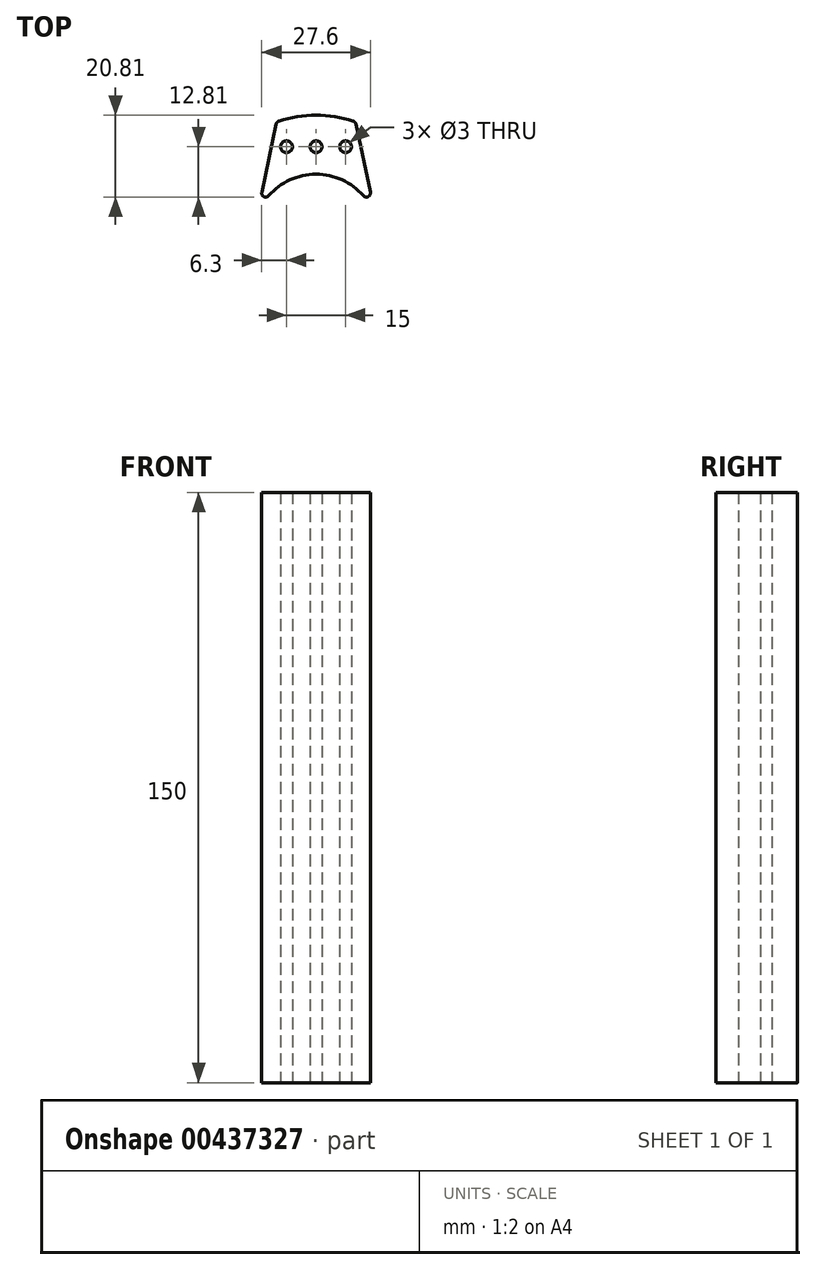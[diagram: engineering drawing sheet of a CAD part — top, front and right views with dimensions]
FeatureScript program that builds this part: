
annotation { "Feature Type Name" : "Feature", "Feature Type Description" : "" }
export const myFeature = defineFeature(function(context is Context, id is Id, definition is map)
    precondition{}
    {
        {
            var Q0;
            Q0=qCreatedBy(makeId("Top.planeOp"),FACE);
            var sketch = newSketch(context, id + "F0", { "sketchPlane" : qUnion([Q0])});
            skArc(sketch, "E0", {"start": v(12.04, 10.53) * mm, "mid": v(0, 16) * mm, "end": v(-12.04, 10.53) * mm});
            skLineSegment(sketch, "E1", {"start": v(-10.12, 28.78) * mm, "end": v(-13.77, 11.4) * mm});
            skLineSegment(sketch, "E2", {"start": v(10.12, 28.78) * mm, "end": v(13.77, 11.4) * mm});
            skArc(sketch, "E3.trimOffspring", {"start": v(9.44, 29.53) * mm, "mid": v(0, 31) * mm, "end": v(-9.44, 29.53) * mm});
            skPoint(sketch, "E4.visualSharp", {"position": v(-15, 5.57) * mm});
            skArc(sketch, "E4.filletArc", {"start": v(-13.77, 11.4) * mm, "mid": v(-13.24, 10.3) * mm, "end": v(-12.04, 10.53) * mm});
            skPoint(sketch, "E5.visualSharp", {"position": v(15, 5.57) * mm});
            skArc(sketch, "E5.filletArc", {"start": v(12.04, 10.53) * mm, "mid": v(13.24, 10.3) * mm, "end": v(13.77, 11.4) * mm});
            skPoint(sketch, "E6.visualSharp", {"position": v(-10, 29.34) * mm});
            skArc(sketch, "E6.filletArc", {"start": v(-9.44, 29.53) * mm, "mid": v(-9.88, 29.24) * mm, "end": v(-10.12, 28.78) * mm});
            skPoint(sketch, "E7.visualSharp", {"position": v(10, 29.34) * mm});
            skArc(sketch, "E7.filletArc", {"start": v(10.12, 28.78) * mm, "mid": v(9.88, 29.24) * mm, "end": v(9.44, 29.53) * mm});
            skCircle(sketch, "E8", {"center": v(0, 23) * mm, "radius": 1.5 * mm});
            skPoint(sketch, "E8.centerSnap0", {"position": v(0, 16) * mm});
            skCircle(sketch, "E9", {"center": v(-7.5, 23) * mm, "radius": 1.5 * mm});
            skLineSegment(sketch, "E10", {"start": v(0, 16) * mm, "end": v(0, 48.83) * mm});
            skCircle(sketch, "E11.MirrorC", {"center": v(7.5, 23) * mm, "radius": 1.5 * mm});
            skSolve(sketch);
        }
        {
            var Q0;
            Q0=makeQuery(id+"F0.imprint","IMPRINT",FACE,{"disambiguationData":[TD([[makeQuery(id+"F0.imprint","IMPRINT",EDGE,{"derivedFrom":sQuery(id+"F0.wireOp",EDGE,"E2")}),-1.0]])]});
            var Q1;
            Q1=makeQuery(id+"F0.imprint","IMPRINT",FACE,{"disambiguationData":[TD([[makeQuery(id+"F0.imprint","IMPRINT",EDGE,{"derivedFrom":sQuery(id+"F0.wireOp",EDGE,"E1")}),1.0]])]});
            extrude(context, id + "F1", {"entities" : qUnion([Q0, Q1]), "depth" : 150 * mm});
        }
    });
